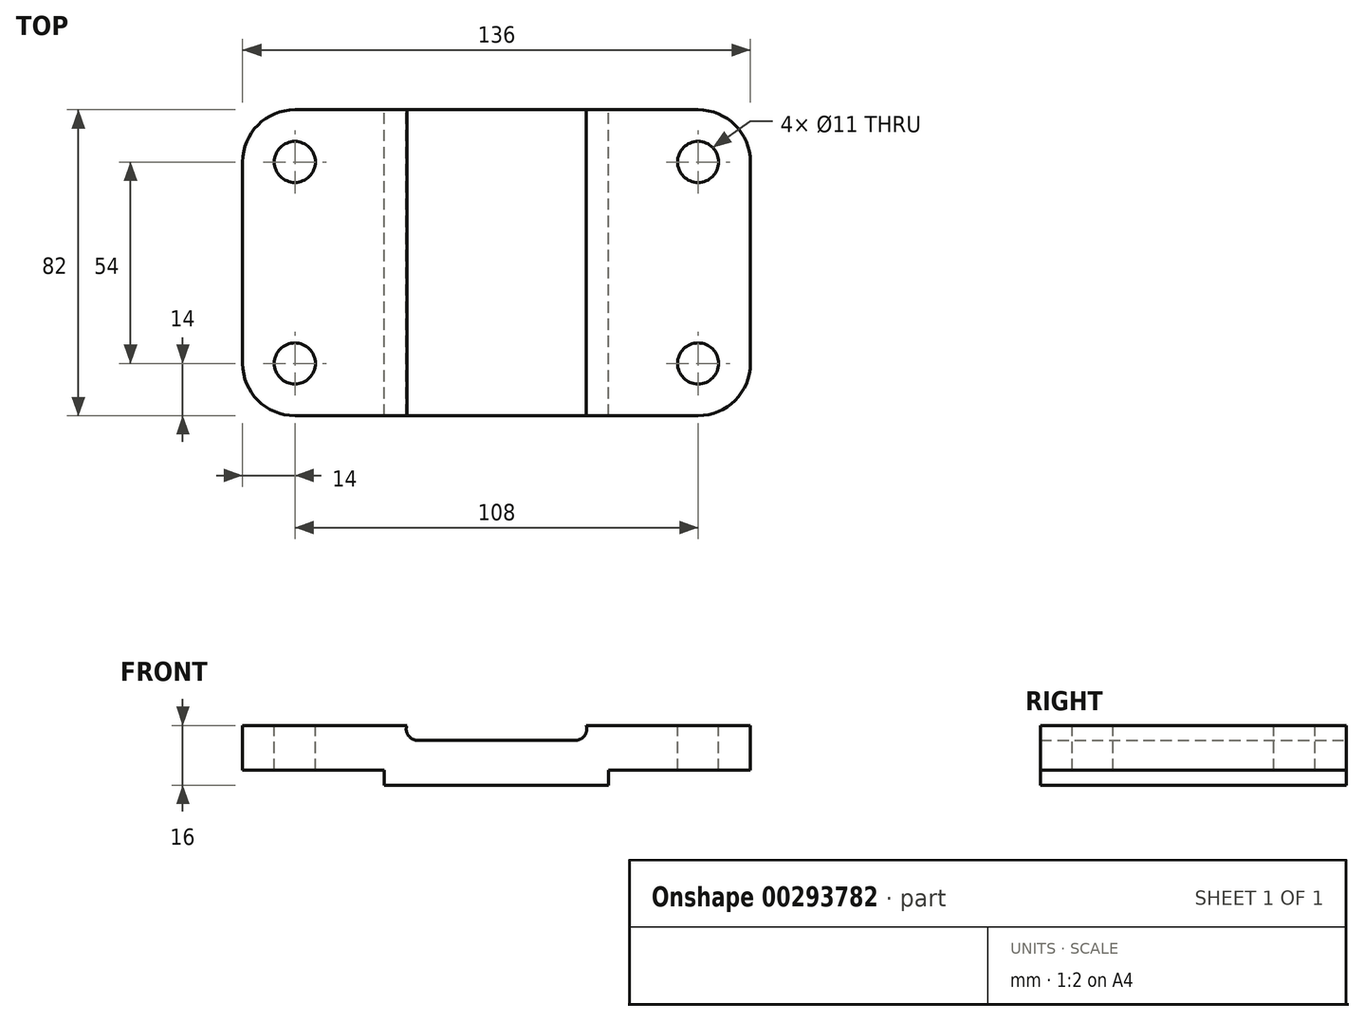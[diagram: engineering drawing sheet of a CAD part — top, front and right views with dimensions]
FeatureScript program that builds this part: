
annotation { "Feature Type Name" : "Feature", "Feature Type Description" : "" }
export const myFeature = defineFeature(function(context is Context, id is Id, definition is map)
    precondition{}
    {
        {
            var Q0;
            Q0=qCreatedBy(makeId("Top.planeOp"),FACE);
            var sketch = newSketch(context, id + "F0", { "sketchPlane" : qUnion([Q0])});
            skLineSegment(sketch, "E0", {"start": v(0, 0) * mm, "end": v(108, 0) * mm});
            skLineSegment(sketch, "E1", {"start": v(-14, -14) * mm, "end": v(-14, -68) * mm});
            skLineSegment(sketch, "E2", {"start": v(0, -82) * mm, "end": v(108, -82) * mm});
            skLineSegment(sketch, "E3", {"start": v(122, -68) * mm, "end": v(122, -14) * mm});
            skArc(sketch, "E4", {"start": v(0, 0) * mm, "mid": v(-9.9, -4.1) * mm, "end": v(-14, -14) * mm});
            skArc(sketch, "E5", {"start": v(0, -82) * mm, "mid": v(-9.9, -77.9) * mm, "end": v(-14, -68) * mm});
            skArc(sketch, "E6", {"start": v(122, -14) * mm, "mid": v(117.9, -4.1) * mm, "end": v(108, 0) * mm});
            skArc(sketch, "E7", {"start": v(122, -68) * mm, "mid": v(117.9, -77.9) * mm, "end": v(108, -82) * mm});
            skLineSegment(sketch, "E8.bottom", {"start": v(0, -14) * mm, "end": v(108, -14) * mm, "construction": true});
            skLineSegment(sketch, "E8.left", {"start": v(0, -14) * mm, "end": v(0, -68) * mm, "construction": true});
            skLineSegment(sketch, "E8.right", {"start": v(108, -14) * mm, "end": v(108, -68) * mm, "construction": true});
            skLineSegment(sketch, "E9", {"start": v(-35.43, -14) * mm, "end": v(148.7, -14) * mm, "construction": true});
            skLineSegment(sketch, "E10", {"start": v(0, -68) * mm, "end": v(108, -68) * mm, "construction": true});
            skLineSegment(sketch, "E11", {"start": v(-42, -68) * mm, "end": v(142.58, -68) * mm, "construction": true});
            skCircle(sketch, "E12", {"center": v(0, -14) * mm, "radius": 5.5 * mm});
            skCircle(sketch, "E13", {"center": v(0, -68) * mm, "radius": 5.5 * mm});
            skCircle(sketch, "E14", {"center": v(108, -14) * mm, "radius": 5.5 * mm});
            skCircle(sketch, "E15", {"center": v(108, -68) * mm, "radius": 5.5 * mm});
            skLineSegment(sketch, "E16", {"start": v(0, 16.84) * mm, "end": v(0, -90.72) * mm, "construction": true});
            skLineSegment(sketch, "E17", {"start": v(108, 10.4) * mm, "end": v(108, -90.72) * mm, "construction": true});
            skSolve(sketch);
        }
        {
            var Q0;
            Q0 = qSketchRegion(id + "F0", true);
            extrude(context, id + "F1", {"entities" : qUnion([Q0]), "oppositeDirection" : true, "depth" : 16 * mm});
        }
        {
            var Q0;
            Q0=qCreatedBy(makeId("Front.planeOp"),FACE);
            var sketch = newSketch(context, id + "F2", { "sketchPlane" : qUnion([Q0])});
            skLineSegment(sketch, "E18", {"start": v(-14, 0) * mm, "end": v(30, 0) * mm});
            skLineSegment(sketch, "E19", {"start": v(122, 0) * mm, "end": v(78, 0) * mm});
            skLineSegment(sketch, "E20", {"start": v(32.83, -4) * mm, "end": v(75.17, -4) * mm});
            skArc(sketch, "E21", {"start": v(32.83, -4) * mm, "mid": v(30.38, -2.73) * mm, "end": v(30, 0) * mm});
            skArc(sketch, "E22", {"start": v(75.17, -4) * mm, "mid": v(77.62, -2.73) * mm, "end": v(78, 0) * mm});
            skLineSegment(sketch, "E23", {"start": v(30, 0) * mm, "end": v(78, 0) * mm});
            skLineSegment(sketch, "E24", {"start": v(-14, -16) * mm, "end": v(24, -16) * mm});
            skLineSegment(sketch, "E25", {"start": v(122, -16) * mm, "end": v(84, -16) * mm});
            skLineSegment(sketch, "E26", {"start": v(-14, -16) * mm, "end": v(-14, -12) * mm});
            skLineSegment(sketch, "E27", {"start": v(-14, -12) * mm, "end": v(24, -12) * mm});
            skLineSegment(sketch, "E28", {"start": v(24, -12) * mm, "end": v(24, -16) * mm});
            skLineSegment(sketch, "E29", {"start": v(84, -16) * mm, "end": v(84, -12) * mm});
            skLineSegment(sketch, "E30", {"start": v(84, -12) * mm, "end": v(122, -12) * mm});
            skLineSegment(sketch, "E31", {"start": v(122, -12) * mm, "end": v(122, -16) * mm});
            skSolve(sketch);
        }
        {
            var Q0;
            Q0 = qSketchRegion(id + "F2", true);
            extrude(context, id + "F3", {"entities" : qUnion([Q0]), "operationType" : NewBodyOperationType.REMOVE, "endBound" : BoundingType.THROUGH_ALL, "depth" : 25 * mm});
        }
    });
